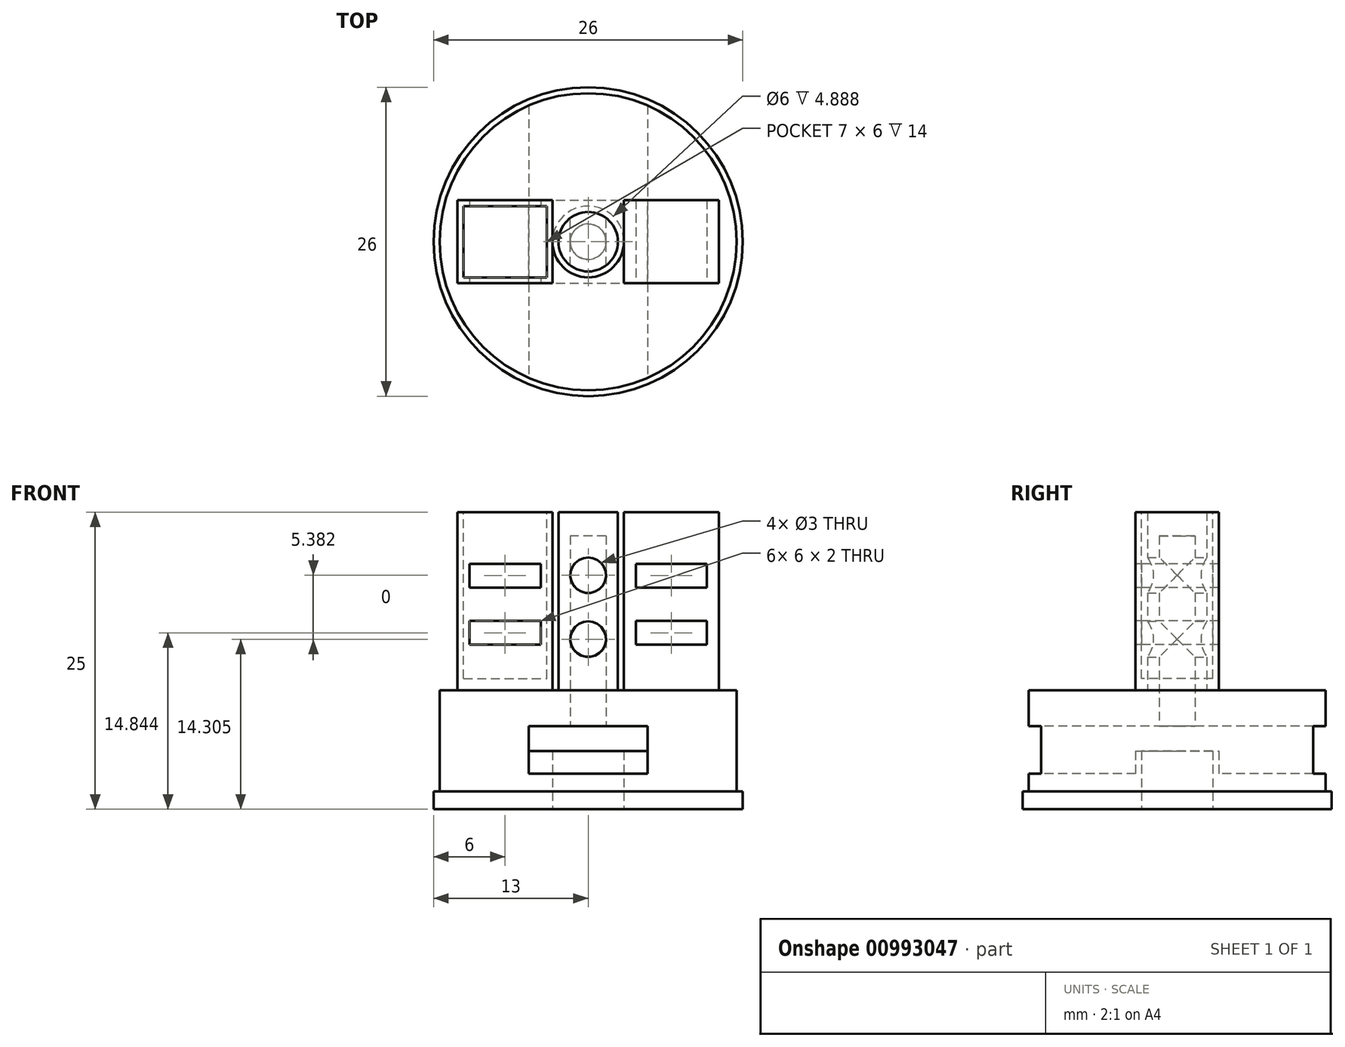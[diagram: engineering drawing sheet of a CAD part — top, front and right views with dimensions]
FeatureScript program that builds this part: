
annotation { "Feature Type Name" : "Feature", "Feature Type Description" : "" }
export const myFeature = defineFeature(function(context is Context, id is Id, definition is map)
    precondition{}
    {
        {
            var Q0;
            Q0=qCreatedBy(makeId("Top.planeOp"),FACE);
            var sketch = newSketch(context, id + "F0", { "sketchPlane" : qUnion([Q0])});
            skCircle(sketch, "E0", {"center": v(0, 0) * mm, "radius": 13 * mm});
            skSolve(sketch);
        }
        {
            var Q0;
            Q0=qCreatedBy(makeId("Top.planeOp"),FACE);
            var sketch = newSketch(context, id + "F1", { "sketchPlane" : qUnion([Q0])});
            skCircle(sketch, "E1", {"center": v(0, 0) * mm, "radius": 12.5 * mm});
            skSolve(sketch);
        }
        {
            var Q0;
            Q0 = qSketchRegion(id + "F0", true);
            extrude(context, id + "F2", {"entities" : qUnion([Q0]), "depth" : 1.5 * mm, "offsetDistance" : 25 * mm});
        }
        {
            var Q0;
            Q0 = qSketchRegion(id + "F1", true);
            extrude(context, id + "F3", {"entities" : qUnion([Q0]), "operationType" : NewBodyOperationType.ADD, "depth" : 10 * mm, "offsetDistance" : 25 * mm});
        }
        {
            var Q0;
            Q0=qCreatedBy(makeId("Top.planeOp"),FACE);
            var sketch = newSketch(context, id + "F4", { "sketchPlane" : qUnion([Q0])});
            skCircle(sketch, "E2", {"center": v(0, 0) * mm, "radius": 2.5 * mm});
            skSolve(sketch);
        }
        {
            var Q0;
            Q0 = qSketchRegion(id + "F4", true);
            extrude(context, id + "F5", {"entities" : qUnion([Q0]), "operationType" : NewBodyOperationType.ADD, "depth" : 25 * mm, "offsetDistance" : 25 * mm});
        }
        {
            var Q0;
            Q0=qCreatedBy(makeId("Top.planeOp"),FACE);
            var sketch = newSketch(context, id + "F6", { "sketchPlane" : qUnion([Q0])});
            skCircle(sketch, "E3", {"center": v(0, 0) * mm, "radius": 1.5 * mm});
            skSolve(sketch);
        }
        {
            var Q0;
            Q0 = qSketchRegion(id + "F6", true);
            extrude(context, id + "F7", {"entities" : qUnion([Q0]), "operationType" : NewBodyOperationType.REMOVE, "depth" : 23 * mm, "offsetDistance" : 25 * mm, "hasSecondDirection" : true, "secondDirectionOppositeDirection" : false, "secondDirectionDepth" : 4 * mm});
        }
        {
            var Q0;
            Q0=qCreatedBy(makeId("Front.planeOp"),FACE);
            var sketch = newSketch(context, id + "F8", { "sketchPlane" : qUnion([Q0])});
            skCircle(sketch, "E4", {"center": v(0, 19.69) * mm, "radius": 1.5 * mm});
            skCircle(sketch, "E5", {"center": v(0, 14.3) * mm, "radius": 1.5 * mm});
            skSolve(sketch);
        }
        {
            var Q0;
            Q0 = qSketchRegion(id + "F8", true);
            extrude(context, id + "F9", {"entities" : qUnion([Q0]), "operationType" : NewBodyOperationType.REMOVE, "endBound" : BoundingType.SYMMETRIC, "depth" : 10.2 * mm, "offsetDistance" : 25 * mm});
        }
        {
            var Q0;
            Q0=qCreatedBy(makeId("Top.planeOp"),FACE);
            var sketch = newSketch(context, id + "F10", { "sketchPlane" : qUnion([Q0])});
            skLineSegment(sketch, "E6.bottom", {"start": v(-3, 3.5) * mm, "end": v(3, 3.5) * mm, "construction": true});
            skLineSegment(sketch, "E6.top", {"start": v(-3, -3.5) * mm, "end": v(3, -3.5) * mm, "construction": true});
            skLineSegment(sketch, "E6.left", {"start": v(-3, 3.5) * mm, "end": v(-3, -3.5) * mm, "construction": true});
            skLineSegment(sketch, "E6.right", {"start": v(3, 3.5) * mm, "end": v(3, -3.5) * mm, "construction": true});
            skPoint(sketch, "E6.middle", {"position": v(0, 0) * mm});
            skLineSegment(sketch, "E7.bottom", {"start": v(-3, -3.5) * mm, "end": v(-11, -3.5) * mm});
            skLineSegment(sketch, "E7.top", {"start": v(-3, 3.5) * mm, "end": v(-11, 3.5) * mm});
            skLineSegment(sketch, "E7.left", {"start": v(-3, -3.5) * mm, "end": v(-3, 3.5) * mm});
            skLineSegment(sketch, "E7.right", {"start": v(-11, -3.5) * mm, "end": v(-11, 3.5) * mm});
            skSolve(sketch);
        }
        {
            var Q0;
            Q0 = qSketchRegion(id + "F10", true);
            extrude(context, id + "F11", {"entities" : qUnion([Q0]), "operationType" : NewBodyOperationType.ADD, "depth" : 25 * mm, "offsetDistance" : 25 * mm});
        }
        {
            var Q0;
            Q0=makeQuery(id+"F11.opExtrude","CAP_FACE",FACE,{"disambiguationData":[OSD([sQuery(id+"F10.wireOp",EDGE,"E7.bottom"),sQuery(id+"F10.wireOp",EDGE,"E7.top"),sQuery(id+"F10.wireOp",EDGE,"E7.left"),sQuery(id+"F10.wireOp",EDGE,"E7.right")])],"isStart":false});
            cPlane(context, id + "F12", {"entities" : qUnion([Q0]), "cplaneType" : CPlaneType.OFFSET, "offset" : 0 * mm, "width" : 150 * mm, "height" : 150 * mm});
        }
        {
            var Q0;
            Q0=qCreatedBy(id+"F12.planeOp",FACE);
            var sketch = newSketch(context, id + "F13", { "sketchPlane" : qUnion([Q0])});
            skLineSegment(sketch, "E8.bottom", {"start": v(-10.48, 3) * mm, "end": v(-3.48, 3) * mm});
            skLineSegment(sketch, "E8.top", {"start": v(-10.48, -3) * mm, "end": v(-3.48, -3) * mm});
            skLineSegment(sketch, "E8.left", {"start": v(-10.48, 3) * mm, "end": v(-10.48, -3) * mm});
            skLineSegment(sketch, "E8.right", {"start": v(-3.48, 3) * mm, "end": v(-3.48, -3) * mm});
            skPoint(sketch, "E8.middle", {"position": v(-6.98, 0) * mm});
            skSolve(sketch);
        }
        {
            var Q0;
            Q0 = qSketchRegion(id + "F13", true);
            extrude(context, id + "F14", {"entities" : qUnion([Q0]), "operationType" : NewBodyOperationType.REMOVE, "oppositeDirection" : true, "depth" : 14 * mm, "offsetDistance" : 25 * mm});
        }
        {
            var Q0;
            Q0=qCreatedBy(makeId("Top.planeOp"),FACE);
            var sketch = newSketch(context, id + "F15", { "sketchPlane" : qUnion([Q0])});
            skLineSegment(sketch, "E9.0", {"start": v(-3, -3.5) * mm, "end": v(-11, -3.5) * mm, "construction": true});
            skLineSegment(sketch, "E9.1", {"start": v(-3, 3.5) * mm, "end": v(-11, 3.5) * mm, "construction": true});
            skLineSegment(sketch, "E9.2", {"start": v(-3, -3.5) * mm, "end": v(-3, 3.5) * mm, "construction": true});
            skLineSegment(sketch, "E10.MirrorCS", {"start": v(3, 3.5) * mm, "end": v(11, 3.5) * mm});
            skLineSegment(sketch, "E11.MirrorCS", {"start": v(3, -3.5) * mm, "end": v(11, -3.5) * mm});
            skLineSegment(sketch, "E12.MirrorCS", {"start": v(3, -3.5) * mm, "end": v(3, 3.5) * mm});
            skLineSegment(sketch, "E13", {"start": v(11, -3.5) * mm, "end": v(11, 3.5) * mm});
            skSolve(sketch);
        }
        {
            var Q0;
            Q0 = qSketchRegion(id + "F15", true);
            extrude(context, id + "F16", {"entities" : qUnion([Q0]), "operationType" : NewBodyOperationType.REMOVE, "depth" : 25 * mm, "offsetDistance" : 25 * mm, "hasSecondDirection" : true, "secondDirectionOppositeDirection" : false, "secondDirectionDepth" : 3 * mm});
        }
        {
            var Q0;
            Q0=qCreatedBy(makeId("Top.planeOp"),FACE);
            var sketch = newSketch(context, id + "F17", { "sketchPlane" : qUnion([Q0])});
            skLineSegment(sketch, "E14.0.0", {"start": v(3, 3.5) * mm, "end": v(3, -3.5) * mm, "construction": true});
            skLineSegment(sketch, "E14.0.1", {"start": v(3, -3.5) * mm, "end": v(11, -3.5) * mm, "construction": true});
            skLineSegment(sketch, "E14.0.2", {"start": v(11, -3.5) * mm, "end": v(11, 3.5) * mm, "construction": true});
            skLineSegment(sketch, "E14.0.3", {"start": v(11, 3.5) * mm, "end": v(3, 3.5) * mm, "construction": true});
            skLineSegment(sketch, "E15.bottom", {"start": v(11, -3.5) * mm, "end": v(3, -3.5) * mm});
            skLineSegment(sketch, "E15.top", {"start": v(11, 3.5) * mm, "end": v(3, 3.5) * mm});
            skLineSegment(sketch, "E15.left", {"start": v(11, -3.5) * mm, "end": v(11, 3.5) * mm});
            skLineSegment(sketch, "E15.right", {"start": v(3, -3.5) * mm, "end": v(3, 3.5) * mm});
            skSolve(sketch);
        }
        {
            var Q0;
            Q0 = qSketchRegion(id + "F17", true);
            extrude(context, id + "F18", {"entities" : qUnion([Q0]), "depth" : 25 * mm, "offsetDistance" : 25 * mm, "hasSecondDirection" : true, "secondDirectionOppositeDirection" : false, "secondDirectionDepth" : 2.8 * mm});
        }
        {
            var Q0;
            Q0=qCreatedBy(makeId("Front.planeOp"),FACE);
            var sketch = newSketch(context, id + "F19", { "sketchPlane" : qUnion([Q0])});
            skLineSegment(sketch, "E16.bottom", {"start": v(-5, 7) * mm, "end": v(5, 7) * mm, "construction": true});
            skLineSegment(sketch, "E16.top", {"start": v(-5, -7) * mm, "end": v(5, -7) * mm, "construction": true});
            skLineSegment(sketch, "E16.left", {"start": v(-5, 7) * mm, "end": v(-5, -7) * mm, "construction": true});
            skLineSegment(sketch, "E16.right", {"start": v(5, 7) * mm, "end": v(5, -7) * mm, "construction": true});
            skPoint(sketch, "E16.middle", {"position": v(0, 0) * mm});
            skLineSegment(sketch, "E17.bottom", {"start": v(5, 7) * mm, "end": v(-5, 7) * mm});
            skLineSegment(sketch, "E17.top", {"start": v(5, 3) * mm, "end": v(-5, 3) * mm});
            skLineSegment(sketch, "E17.left", {"start": v(5, 7) * mm, "end": v(5, 3) * mm});
            skLineSegment(sketch, "E17.right", {"start": v(-5, 7) * mm, "end": v(-5, 3) * mm});
            skSolve(sketch);
        }
        {
            var Q0;
            Q0 = qSketchRegion(id + "F19", true);
            extrude(context, id + "F20", {"entities" : qUnion([Q0]), "operationType" : NewBodyOperationType.REMOVE, "endBound" : BoundingType.SYMMETRIC, "oppositeDirection" : true, "depth" : 28 * mm, "offsetDistance" : 25 * mm});
        }
        {
            var Q0;
            Q0=qCreatedBy(makeId("Front.planeOp"),FACE);
            var sketch = newSketch(context, id + "F21", { "sketchPlane" : qUnion([Q0])});
            skLineSegment(sketch, "E18.bottom", {"start": v(-5, 4.89) * mm, "end": v(5, 4.89) * mm});
            skLineSegment(sketch, "E18.top", {"start": v(-5, 2.89) * mm, "end": v(5, 2.89) * mm});
            skLineSegment(sketch, "E18.left", {"start": v(-5, 4.89) * mm, "end": v(-5, 2.89) * mm});
            skLineSegment(sketch, "E18.right", {"start": v(5, 4.89) * mm, "end": v(5, 2.89) * mm});
            skPoint(sketch, "E18.middle", {"position": v(0, 3.89) * mm});
            skSolve(sketch);
        }
        {
            var Q0;
            Q0 = qSketchRegion(id + "F21", true);
            extrude(context, id + "F22", {"entities" : qUnion([Q0]), "operationType" : NewBodyOperationType.ADD, "endBound" : BoundingType.SYMMETRIC, "depth" : 7 * mm, "offsetDistance" : 25 * mm});
        }
        {
            var Q0;
            Q0=qCreatedBy(makeId("Top.planeOp"),FACE);
            var sketch = newSketch(context, id + "F23", { "sketchPlane" : qUnion([Q0])});
            skCircle(sketch, "E19", {"center": v(0, 0) * mm, "radius": 3 * mm});
            skSolve(sketch);
        }
        {
            var Q0;
            Q0 = qSketchRegion(id + "F23", true);
            extrude(context, id + "F24", {"entities" : qUnion([Q0]), "operationType" : NewBodyOperationType.REMOVE, "depth" : 5.2 * mm, "offsetDistance" : 25 * mm});
        }
        {
            var Q0;
            Q0=makeQuery(id+"F11.opExtrude","SWEPT_FACE",FACE,{"disambiguationData":[OSD([sQuery(id+"F10.wireOp",EDGE,"E7.bottom")])]});
            cPlane(context, id + "F25", {"entities" : qUnion([Q0]), "cplaneType" : CPlaneType.OFFSET, "offset" : 1 * mm, "width" : 150 * mm, "height" : 150 * mm});
        }
        {
            var Q0;
            Q0=qCreatedBy(id+"F25.planeOp",FACE);
            var sketch = newSketch(context, id + "F26", { "sketchPlane" : qUnion([Q0])});
            skLineSegment(sketch, "E20.bottom", {"start": v(-10, 20.65) * mm, "end": v(-4, 20.65) * mm});
            skLineSegment(sketch, "E20.top", {"start": v(-10, 18.65) * mm, "end": v(-4, 18.65) * mm});
            skLineSegment(sketch, "E20.left", {"start": v(-10, 20.65) * mm, "end": v(-10, 18.65) * mm});
            skLineSegment(sketch, "E20.right", {"start": v(-4, 20.65) * mm, "end": v(-4, 18.65) * mm});
            skPoint(sketch, "E20.middle", {"position": v(-7, 19.65) * mm});
            skLineSegment(sketch, "E21.bottom", {"start": v(-10, 15.84) * mm, "end": v(-4, 15.84) * mm});
            skLineSegment(sketch, "E21.top", {"start": v(-10, 13.84) * mm, "end": v(-4, 13.84) * mm});
            skLineSegment(sketch, "E21.left", {"start": v(-10, 15.84) * mm, "end": v(-10, 13.84) * mm});
            skLineSegment(sketch, "E21.right", {"start": v(-4, 15.84) * mm, "end": v(-4, 13.84) * mm});
            skPoint(sketch, "E21.middle", {"position": v(-7, 14.84) * mm});
            skLineSegment(sketch, "E22.MirrorCS", {"start": v(10, 20.65) * mm, "end": v(4, 20.65) * mm});
            skLineSegment(sketch, "E23.MirrorCS", {"start": v(10, 18.65) * mm, "end": v(4, 18.65) * mm});
            skLineSegment(sketch, "E24.MirrorCS", {"start": v(4, 20.65) * mm, "end": v(4, 18.65) * mm});
            skLineSegment(sketch, "E25.MirrorCS", {"start": v(10, 20.65) * mm, "end": v(10, 18.65) * mm});
            skLineSegment(sketch, "E26.MirrorCS", {"start": v(10, 15.84) * mm, "end": v(10, 13.84) * mm});
            skLineSegment(sketch, "E27.MirrorCS", {"start": v(4, 15.84) * mm, "end": v(4, 13.84) * mm});
            skLineSegment(sketch, "E28.MirrorCS", {"start": v(10, 13.84) * mm, "end": v(4, 13.84) * mm});
            skLineSegment(sketch, "E29.MirrorCS", {"start": v(10, 15.84) * mm, "end": v(4, 15.84) * mm});
            skSolve(sketch);
        }
        {
            var Q0;
            Q0 = qSketchRegion(id + "F26", true);
            extrude(context, id + "F27", {"entities" : qUnion([Q0]), "operationType" : NewBodyOperationType.REMOVE, "oppositeDirection" : true, "depth" : 9 * mm, "offsetDistance" : 25 * mm});
        }
    });
